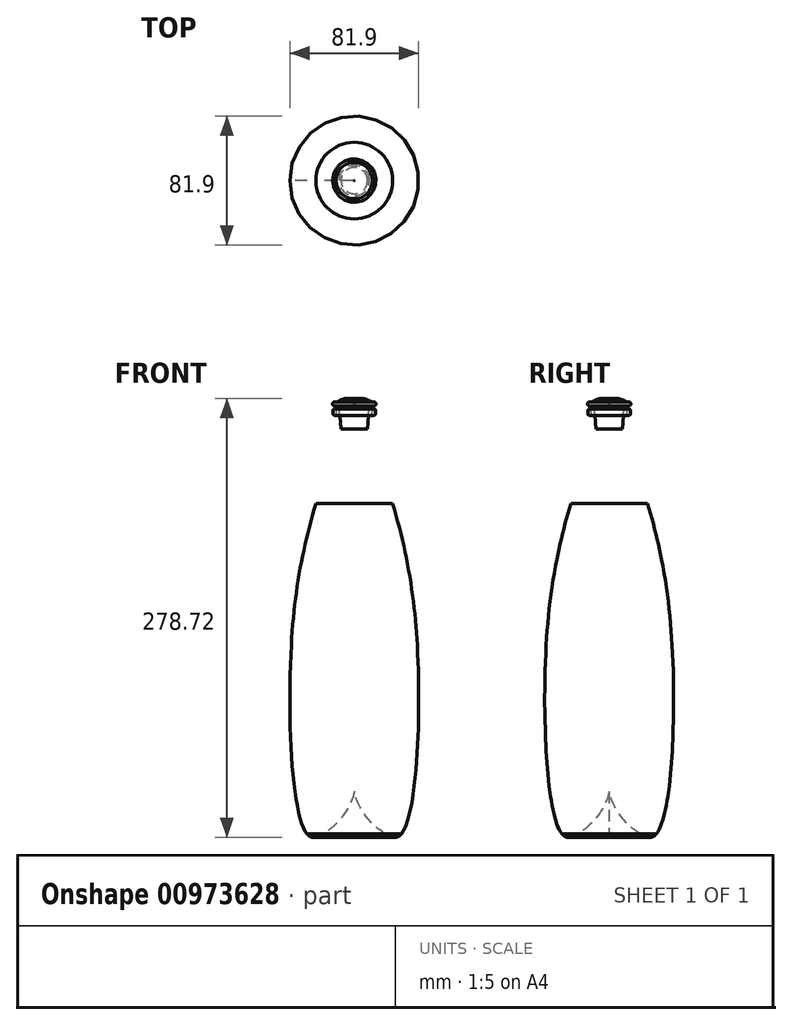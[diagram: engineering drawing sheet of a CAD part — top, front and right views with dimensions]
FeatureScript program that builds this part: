
annotation { "Feature Type Name" : "Feature", "Feature Type Description" : "" }
export const myFeature = defineFeature(function(context is Context, id is Id, definition is map)
    precondition{}
    {
        {
            var Q0;
            Q0=qCreatedBy(makeId("Front.planeOp"),FACE);
            var sketch = newSketch(context, id + "F0", { "sketchPlane" : qUnion([Q0])});
            skLineSegment(sketch, "E0", {"start": v(0, 0) * mm, "end": v(0, 270) * mm});
            skLineSegment(sketch, "E1", {"start": v(-9.5, 270) * mm, "end": v(-8.58, 259.44) * mm});
            skPoint(sketch, "E2", {"position": v(0, 246) * mm});
            skLineSegment(sketch, "E3", {"start": v(-77.67, 256) * mm, "end": v(0, 256) * mm});
            skLineSegment(sketch, "E4", {"start": v(-40, 120) * mm, "end": v(118.95, 120) * mm});
            skLineSegment(sketch, "E5", {"start": v(0, 0) * mm, "end": v(-30, 0) * mm});
            skPoint(sketch, "E6", {"position": v(0, 27) * mm});
            skLineSegment(sketch, "E7", {"start": v(-9.5, 270) * mm, "end": v(0, 270) * mm});
            skPoint(sketch, "E8", {"position": v(-20, 0) * mm});
            skFitSpline(sketch, "E9", {"points": [v(0, 27) * mm, v(-20, 0) * mm, v(-30, 0) * mm, v(-40, 120) * mm, v(-8.28, 256) * mm], "startDerivative": vector(-50.01, -221.22) * mm, "endDerivative": vector(151.7, 395.11) * mm});
            skArc(sketch, "E10.filletArc", {"start": v(-9.5, 252.8) * mm, "mid": v(-8.66, 256.07) * mm, "end": v(-8.58, 259.44) * mm});
            skLineSegment(sketch, "E11", {"start": v(0, 210) * mm, "end": v(-76.1, 210) * mm});
            skPoint(sketch, "E12", {"position": v(-24.3, 210) * mm});
            skSolve(sketch);
        }
        {
            var Q0;
            Q0=qCreatedBy(makeId("Front.planeOp"),FACE);
            var sketch = newSketch(context, id + "F1", { "sketchPlane" : qUnion([Q0])});
            skLineSegment(sketch, "E13.0.0", {"start": v(-40, 120) * mm, "end": v(-42.85, 120) * mm});
            skFitSpline(sketch, "E13.0.1", {"points": [v(-8.28, 256) * mm, v(-27.1, 206.98) * mm, v(-46.24, 138.17) * mm, v(-38.6, -6.34) * mm, v(-17.98, -0.72) * mm, v(-3.04, 13.54) * mm, v(0, 27) * mm]});
            skPoint(sketch, "E14", {"position": v(-25.85, -2.11) * mm});
            skPoint(sketch, "E15", {"position": v(0, 25) * mm});
            skLineSegment(sketch, "E16.0", {"start": v(-11.5, 270) * mm, "end": v(-10.57, 259.26) * mm});
            skArc(sketch, "E17.0", {"start": v(-11.38, 253.49) * mm, "mid": v(-10.64, 256.33) * mm, "end": v(-10.57, 259.26) * mm});
            skPoint(sketch, "E18", {"position": v(-42.85, 120) * mm});
            skPoint(sketch, "E19", {"position": v(-20, -4) * mm});
            skPoint(sketch, "E20", {"position": v(-31.56, -4) * mm});
            skFitSpline(sketch, "E21", {"points": [v(0, 25) * mm, v(-20, -4) * mm, v(-31.56, -4) * mm, v(-42.85, 120) * mm, v(-11.38, 253.49) * mm], "startDerivative": vector(-33.89, -165.62) * mm, "endDerivative": vector(107.89, 254.87) * mm});
            skPoint(sketch, "E22", {"position": v(-26.58, 210) * mm});
            skLineSegment(sketch, "E23.0", {"start": v(-9.45, 269.4) * mm, "end": v(-8.89, 263.03) * mm});
            skPoint(sketch, "E24.0", {"position": v(-8.28, 256) * mm});
            skArc(sketch, "E25.0", {"start": v(-9.5, 252.8) * mm, "mid": v(-8.66, 256.07) * mm, "end": v(-8.58, 259.44) * mm});
            skPoint(sketch, "E26.orphan", {"position": v(-8.58, 259.44) * mm});
            skLineSegment(sketch, "E27.0", {"start": v(-11.5, 270) * mm, "end": v(-10.1, 270) * mm});
            skPoint(sketch, "E28.orphan", {"position": v(0, 270) * mm});
            skPoint(sketch, "E29.visualSharp", {"position": v(-9.5, 270) * mm});
            skArc(sketch, "E29.filletArc", {"start": v(-9.45, 269.4) * mm, "mid": v(-9.66, 269.83) * mm, "end": v(-10.1, 270) * mm});
            skLineSegment(sketch, "E30", {"start": v(-11.5, 270) * mm, "end": v(-12.5, 270) * mm});
            skLineSegment(sketch, "E31", {"start": v(-13.5, 269) * mm, "end": v(-13.5, 267) * mm});
            skLineSegment(sketch, "E32", {"start": v(-12.5, 266) * mm, "end": v(-11.16, 266) * mm});
            skPoint(sketch, "E33.visualSharp", {"position": v(-13.5, 270) * mm});
            skArc(sketch, "E33.filletArc", {"start": v(-12.5, 270) * mm, "mid": v(-13.21, 269.7) * mm, "end": v(-13.5, 269) * mm});
            skPoint(sketch, "E34.visualSharp", {"position": v(-13.5, 266) * mm});
            skArc(sketch, "E34.filletArc", {"start": v(-13.5, 267) * mm, "mid": v(-13.21, 266.3) * mm, "end": v(-12.5, 266) * mm});
            skLineSegment(sketch, "E35", {"start": v(-8.58, 259.44) * mm, "end": v(-8.89, 263.03) * mm});
            skFitSpline(sketch, "E36.0", {"points": [v(0, 27) * mm, v(-3.04, 13.54) * mm, v(-17.98, -0.72) * mm, v(-38.6, -6.34) * mm, v(-46.24, 138.17) * mm, v(-27.1, 206.98) * mm, v(-8.28, 256) * mm]});
            skArc(sketch, "E37", {"start": v(-26.37, 210.72) * mm, "mid": v(-27.3, 210.2) * mm, "end": v(-26.78, 209.28) * mm});
            skArc(sketch, "E38", {"start": v(-43.53, 53.66) * mm, "mid": v(-44.23, 52.87) * mm, "end": v(-43.43, 52.17) * mm});
            skLineSegment(sketch, "E39.trimOffspring", {"start": v(0, 210) * mm, "end": v(0, 270) * mm});
            skPoint(sketch, "E40.orphan", {"position": v(0, 0) * mm});
            skPoint(sketch, "E41.orphan", {"position": v(-30, 0) * mm});
            skArc(sketch, "E42.MirrorCS", {"start": v(13.5, 267) * mm, "mid": v(13.21, 266.3) * mm, "end": v(12.5, 266) * mm});
            skPoint(sketch, "E43.MirrorP", {"position": v(20, -4) * mm});
            skPoint(sketch, "E44.MirrorP", {"position": v(13.5, 266) * mm});
            skLineSegment(sketch, "E45.MirrorCS", {"start": v(12.5, 266) * mm, "end": v(11.16, 266) * mm});
            skLineSegment(sketch, "E46.MirrorCS", {"start": v(11.5, 270) * mm, "end": v(10.57, 259.26) * mm});
            skLineSegment(sketch, "E47.MirrorCS", {"start": v(8.58, 259.44) * mm, "end": v(8.89, 263.03) * mm});
            skFitSpline(sketch, "E48.MirrorCS", {"points": [v(0, 25) * mm, v(20, -4) * mm, v(31.56, -4) * mm, v(42.85, 120) * mm, v(11.38, 253.49) * mm], "startDerivative": vector(33.89, -165.62) * mm, "endDerivative": vector(-107.89, 254.87) * mm});
            skArc(sketch, "E49.MirrorCS", {"start": v(26.37, 210.72) * mm, "mid": v(27.3, 210.2) * mm, "end": v(26.78, 209.28) * mm});
            skPoint(sketch, "E50.MirrorP", {"position": v(8.58, 259.44) * mm});
            skPoint(sketch, "E51.MirrorP", {"position": v(8.28, 256) * mm});
            skArc(sketch, "E52.MirrorCS", {"start": v(12.5, 270) * mm, "mid": v(13.21, 269.7) * mm, "end": v(13.5, 269) * mm});
            skArc(sketch, "E53.MirrorCS", {"start": v(11.38, 253.49) * mm, "mid": v(10.64, 256.33) * mm, "end": v(10.57, 259.26) * mm});
            skFitSpline(sketch, "E54.MirrorCS", {"points": [v(0, 27) * mm, v(3.04, 13.54) * mm, v(17.98, -0.72) * mm, v(38.6, -6.34) * mm, v(46.24, 138.17) * mm, v(27.1, 206.98) * mm, v(8.28, 256) * mm]});
            skLineSegment(sketch, "E55.MirrorCS", {"start": v(11.5, 270) * mm, "end": v(10.1, 270) * mm});
            skArc(sketch, "E56.MirrorCS", {"start": v(9.45, 269.4) * mm, "mid": v(9.66, 269.83) * mm, "end": v(10.1, 270) * mm});
            skPoint(sketch, "E57.MirrorP", {"position": v(25.85, -2.11) * mm});
            skPoint(sketch, "E58.MirrorP", {"position": v(13.5, 270) * mm});
            skPoint(sketch, "E59.MirrorP", {"position": v(9.5, 270) * mm});
            skPoint(sketch, "E60.MirrorP", {"position": v(30, 0) * mm});
            skArc(sketch, "E61.MirrorCS", {"start": v(43.53, 53.66) * mm, "mid": v(44.23, 52.87) * mm, "end": v(43.43, 52.17) * mm});
            skLineSegment(sketch, "E62.MirrorCS", {"start": v(9.45, 269.4) * mm, "end": v(8.89, 263.03) * mm});
            skLineSegment(sketch, "E63.MirrorCS", {"start": v(11.5, 270) * mm, "end": v(12.5, 270) * mm});
            skLineSegment(sketch, "E64.MirrorCS", {"start": v(40, 120) * mm, "end": v(42.85, 120) * mm});
            skArc(sketch, "E65.MirrorCS", {"start": v(9.5, 252.8) * mm, "mid": v(8.66, 256.07) * mm, "end": v(8.58, 259.44) * mm});
            skLineSegment(sketch, "E66.MirrorCS", {"start": v(13.5, 269) * mm, "end": v(13.5, 267) * mm});
            skFitSpline(sketch, "E67.MirrorCS", {"points": [v(8.28, 256) * mm, v(27.1, 206.98) * mm, v(46.24, 138.17) * mm, v(38.6, -6.34) * mm, v(17.98, -0.72) * mm, v(3.04, 13.54) * mm, v(0, 27) * mm]});
            skLineSegment(sketch, "E68", {"start": v(0, 25) * mm, "end": v(0, 27) * mm});
            skLineSegment(sketch, "E69", {"start": v(-51.46, -6.6) * mm, "end": v(50.32, -6.6) * mm});
            skLineSegment(sketch, "E70", {"start": v(50.32, -6.6) * mm, "end": v(-19.35, -6.6) * mm});
            skLineSegment(sketch, "E71", {"start": v(-53.27, 0.4) * mm, "end": v(55.21, 0.4) * mm});
            skSolve(sketch);
        }
        {
            var Q0;
            {var subQ0=sQuery(id+"F0.wireOp",EDGE,"E9");var subQ6=sQuery(id+"F0.wireOp",EDGE,"E0");var subQ8=makeQuery(id+"F0.imprint","INTERSECT",VERTEX,{"derivedFrom":[subQ6,subQ0]});Q0=makeQuery(id+"F0.imprint","IMPRINT",FACE,{"disambiguationData":[TD([[makeQuery(id+"F0.imprint","IMPRINT",EDGE,{"disambiguationData":[TD([[subQ8,-1.0]])],"derivedFrom":subQ6}),1.0]])]});}
            var Q1;
            {var subQ0=sQuery(id+"F0.wireOp",EDGE,"E9");var subQ1=sQuery(id+"F0.wireOp",EDGE,"E5");var subQ2=makeQuery(id+"F0.imprint","INTERSECT",VERTEX,{"disambiguationData":[OD(0.0)],"derivedFrom":[subQ1,subQ0]});Q1=makeQuery(id+"F0.imprint","IMPRINT",FACE,{"disambiguationData":[TD([[makeQuery(id+"F0.imprint","IMPRINT",EDGE,{"disambiguationData":[TD([[subQ2,1.0]])],"derivedFrom":subQ1}),1.0]])]});}
            var Q2;
            {var subQ0=sQuery(id+"F0.wireOp",EDGE,"E11");var subQ1=sQuery(id+"F0.wireOp",EDGE,"E0");var subQ2=makeQuery(id+"F0.imprint","INTERSECT",VERTEX,{"derivedFrom":[subQ1,subQ0]});Q2=makeQuery(id+"F0.imprint","IMPRINT",FACE,{"disambiguationData":[TD([[makeQuery(id+"F0.imprint","IMPRINT",EDGE,{"disambiguationData":[TD([[subQ2,1.0]])],"derivedFrom":subQ1}),1.0]])]});}
            var Q3;
            Q3=sQuery(id+"F0.wireOp",EDGE,"E0");
            revolve(context, id + "F2", {"surfaceOperationType" : NewSurfaceOperationType.NEW, "entities" : qUnion([Q0, Q1, Q2]), "axis" : qUnion([Q3]), "revolveType" : RevolveType.FULL});
        }
        {
            var Q0;
            {var subQ0=sQuery(id+"F1.wireOp",EDGE,"E30");Q0=makeQuery(id+"F1.imprint","IMPRINT",FACE,{"disambiguationData":[TD([[makeQuery(id+"F1.imprint","IMPRINT",EDGE,{"derivedFrom":subQ0}),1.0]])]});}
            var Q1;
            {var subQ3=sQuery(id+"F1.wireOp",EDGE,"E13.0.0");Q1=makeQuery(id+"F1.imprint","IMPRINT",FACE,{"disambiguationData":[TD([[makeQuery(id+"F1.imprint","IMPRINT",EDGE,{"derivedFrom":subQ3}),-1.0]])]});}
            var Q2;
            {var subQ2=sQuery(id+"F1.wireOp",EDGE,"E13.0.0");Q2=makeQuery(id+"F1.imprint","IMPRINT",FACE,{"disambiguationData":[TD([[makeQuery(id+"F1.imprint","IMPRINT",EDGE,{"derivedFrom":subQ2}),1.0]])]});}
            var Q3;
            Q3=sQuery(id+"F1.wireOp",EDGE,"E39.trimOffspring");
            revolve(context, id + "F3", {"surfaceOperationType" : NewSurfaceOperationType.NEW, "entities" : qUnion([Q0, Q1, Q2]), "axis" : qUnion([Q3]), "revolveType" : RevolveType.FULL});
        }
        {
            var Q0;
            Q0=qCreatedBy(makeId("Front.planeOp"),FACE);
            var sketch = newSketch(context, id + "F4", { "sketchPlane" : qUnion([Q0])});
            skLineSegment(sketch, "E72.0", {"start": v(-9.67, 272) * mm, "end": v(-8.4, 257.44) * mm});
            skPoint(sketch, "E73.0", {"position": v(-12.5, 267) * mm});
            skPoint(sketch, "E74.0", {"position": v(-12.5, 269) * mm});
            skLineSegment(sketch, "E75.0", {"start": v(0, 257.44) * mm, "end": v(0, 278.5) * mm});
            skLineSegment(sketch, "E76", {"start": v(-12.5, 272) * mm, "end": v(0, 272) * mm});
            skLineSegment(sketch, "E77", {"start": v(0, 257.44) * mm, "end": v(-8.4, 257.44) * mm});
            skArc(sketch, "E78", {"start": v(-11.54, 274.04) * mm, "mid": v(-13.64, 273.78) * mm, "end": v(-12.5, 272) * mm});
            skPoint(sketch, "E79", {"position": v(-3.02, 276.33) * mm});
            skPoint(sketch, "E80", {"position": v(0, 272) * mm});
            skFitSpline(sketch, "E81", {"points": [v(-12.5, 273.25) * mm, v(-3.02, 276.33) * mm, v(-0.01, 272) * mm], "startDerivative": vector(17.47, 15.6) * mm, "endDerivative": vector(4.06, -16.3) * mm});
            skLineSegment(sketch, "E82.MirrorCS", {"start": v(0, 257.44) * mm, "end": v(8.4, 257.44) * mm});
            skLineSegment(sketch, "E83.MirrorCS", {"start": v(9.67, 272) * mm, "end": v(8.4, 257.44) * mm});
            skLineSegment(sketch, "E84.MirrorCS", {"start": v(12.5, 272) * mm, "end": v(0, 272) * mm});
            skArc(sketch, "E85.MirrorCS", {"start": v(11.54, 274.04) * mm, "mid": v(13.64, 273.78) * mm, "end": v(12.5, 272) * mm});
            skFitSpline(sketch, "E86.MirrorCS", {"points": [v(12.5, 273.25) * mm, v(3.02, 276.33) * mm, v(0.01, 272) * mm], "startDerivative": vector(-17.47, 15.6) * mm, "endDerivative": vector(-4.06, -16.3) * mm});
            skSolve(sketch);
        }
        {
            var Q0;
            {var subQ0=sQuery(id+"F4.wireOp",EDGE,"E76");var subQ1=makeQuery(id+"F4.imprint","INTERSECT",VERTEX,{"derivedFrom":[sQuery(id+"F4.wireOp",EDGE,"E72.0"),subQ0]});Q0=makeQuery(id+"F4.imprint","IMPRINT",FACE,{"disambiguationData":[TD([[makeQuery(id+"F4.imprint","IMPRINT",EDGE,{"disambiguationData":[TD([[subQ1,1.0]])],"derivedFrom":subQ0}),1.0]])]});}
            var Q1;
            {var subQ0=sQuery(id+"F4.wireOp",EDGE,"E78");var subQ1=makeQuery(id+"F4.imprint","INTERSECT",VERTEX,{"derivedFrom":[sQuery(id+"F4.wireOp",EDGE,"E76"),subQ0]});Q1=makeQuery(id+"F4.imprint","IMPRINT",FACE,{"disambiguationData":[TD([[makeQuery(id+"F4.imprint","IMPRINT",EDGE,{"disambiguationData":[TD([[subQ1,1.0]])],"derivedFrom":subQ0}),1.0]])]});}
            var Q2;
            Q2=sQuery(id+"F4.wireOp",EDGE,"E75.0");
            revolve(context, id + "F5", {"surfaceOperationType" : NewSurfaceOperationType.NEW, "entities" : qUnion([Q0, Q1]), "axis" : qUnion([Q2]), "revolveType" : RevolveType.FULL});
        }
        {
            var Q0;
            {var subQ0=sQuery(id+"F4.wireOp",EDGE,"E72.0");Q0=makeQuery(id+"F4.imprint","IMPRINT",FACE,{"disambiguationData":[TD([[makeQuery(id+"F4.imprint","IMPRINT",EDGE,{"derivedFrom":subQ0}),1.0]])]});}
            var Q1;
            Q1=sQuery(id+"F4.wireOp",EDGE,"E75.0");
            revolve(context, id + "F6", {"surfaceOperationType" : NewSurfaceOperationType.NEW, "entities" : qUnion([Q0]), "axis" : qUnion([Q1]), "revolveType" : RevolveType.FULL});
        }
    });
